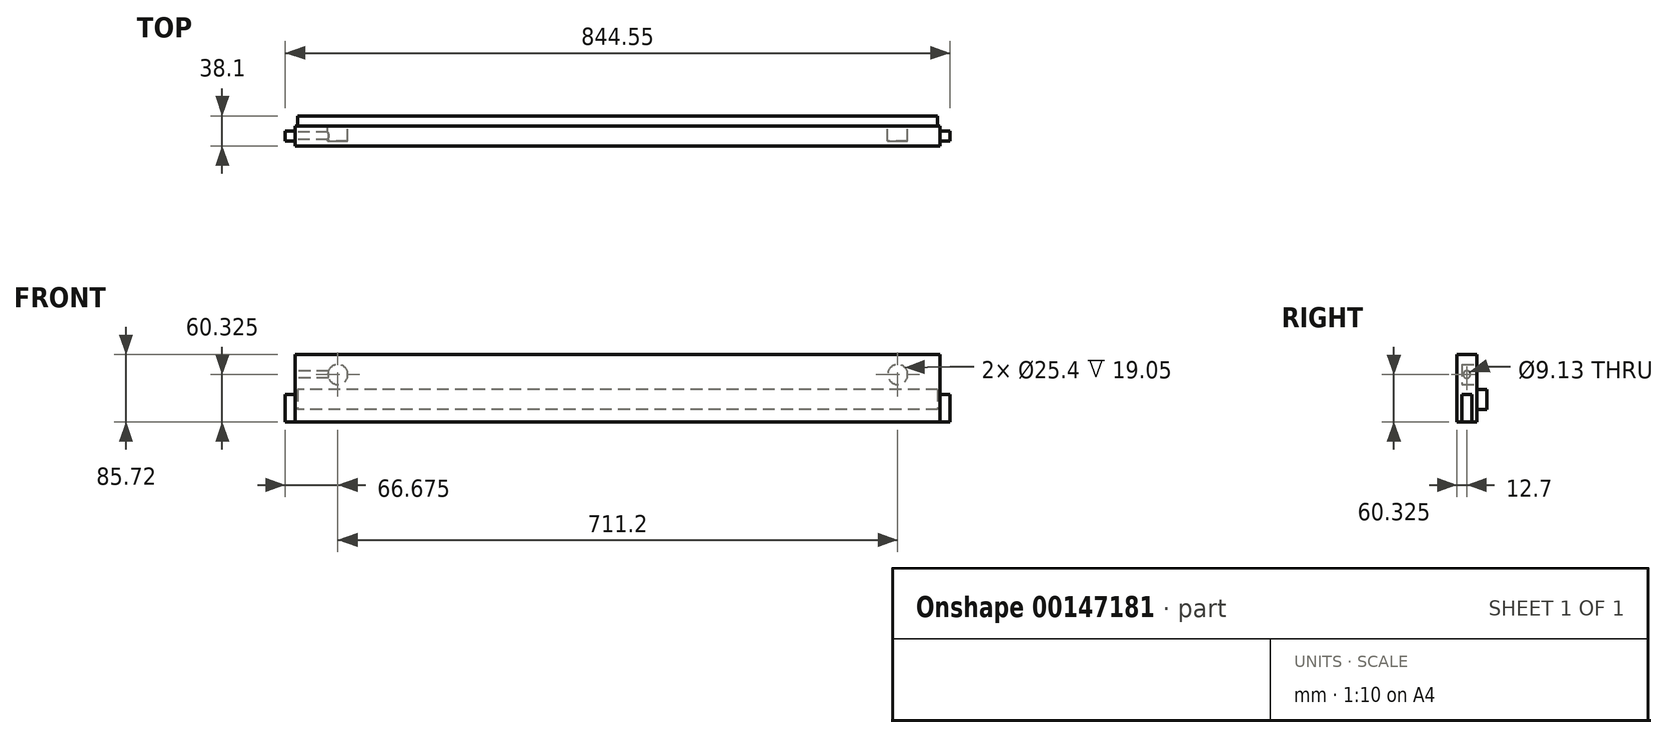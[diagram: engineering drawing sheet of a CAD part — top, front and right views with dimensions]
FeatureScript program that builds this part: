
annotation { "Feature Type Name" : "Feature", "Feature Type Description" : "" }
export const myFeature = defineFeature(function(context is Context, id is Id, definition is map)
    precondition{}
    {
        {
            var Q0;
            Q0=qCreatedBy(makeId("Front.planeOp"),FACE);
            var sketch = newSketch(context, id + "F0", { "sketchPlane" : qUnion([Q0])});
            skLineSegment(sketch, "E0.bottom", {"start": v(0, 0) * mm, "end": v(844.55, 0) * mm});
            skLineSegment(sketch, "E0.top", {"start": v(0, 85.73) * mm, "end": v(844.55, 85.73) * mm});
            skLineSegment(sketch, "E0.left", {"start": v(0, 0) * mm, "end": v(0, 85.73) * mm});
            skLineSegment(sketch, "E0.right", {"start": v(844.55, 0) * mm, "end": v(844.55, 85.73) * mm});
            skSolve(sketch);
        }
        {
            var Q0;
            Q0=makeQuery(id+"F0.imprint","IMPRINT",FACE,{"disambiguationData":[TD([[makeQuery(id+"F0.imprint","IMPRINT",EDGE,{"derivedFrom":sQuery(id+"F0.wireOp",EDGE,"E0.bottom")}),1.0]])]});
            extrude(context, id + "F1", {"entities" : qUnion([Q0]), "depth" : 25.4 * mm});
        }
        {
            var Q0;
            Q0=makeQuery(id+"F1.opExtrude","CAP_FACE",FACE,{"disambiguationData":[OSD([sQuery(id+"F0.wireOp",EDGE,"E0.bottom"),sQuery(id+"F0.wireOp",EDGE,"E0.top"),sQuery(id+"F0.wireOp",EDGE,"E0.left"),sQuery(id+"F0.wireOp",EDGE,"E0.right")])],"isStart":false});
            var sketch = newSketch(context, id + "F2", { "sketchPlane" : qUnion([Q0])});
            skLineSegment(sketch, "E1.bottom", {"start": v(0, 85.73) * mm, "end": v(12.7, 85.73) * mm});
            skLineSegment(sketch, "E1.top", {"start": v(0, 34.93) * mm, "end": v(12.7, 34.93) * mm});
            skLineSegment(sketch, "E1.left", {"start": v(0, 85.73) * mm, "end": v(0, 34.93) * mm});
            skLineSegment(sketch, "E1.right", {"start": v(12.7, 85.73) * mm, "end": v(12.7, 34.92) * mm});
            skLineSegment(sketch, "E2.bottom", {"start": v(831.85, 85.73) * mm, "end": v(844.55, 85.73) * mm});
            skLineSegment(sketch, "E2.top", {"start": v(831.85, 34.92) * mm, "end": v(844.55, 34.92) * mm});
            skLineSegment(sketch, "E2.left", {"start": v(831.85, 85.73) * mm, "end": v(831.85, 34.92) * mm});
            skLineSegment(sketch, "E2.right", {"start": v(844.55, 85.73) * mm, "end": v(844.55, 34.93) * mm});
            skSolve(sketch);
        }
        {
            var Q0;
            Q0=makeQuery(id+"F2.imprint","IMPRINT",FACE,{"disambiguationData":[TD([[makeQuery(id+"F2.imprint","IMPRINT",EDGE,{"derivedFrom":sQuery(id+"F2.wireOp",EDGE,"E1.bottom")}),-1.0]])]});
            var Q1;
            Q1=makeQuery(id+"F2.imprint","IMPRINT",FACE,{"disambiguationData":[TD([[makeQuery(id+"F2.imprint","IMPRINT",EDGE,{"derivedFrom":sQuery(id+"F2.wireOp",EDGE,"E2.bottom")}),-1.0]])]});
            extrude(context, id + "F3", {"entities" : qUnion([Q0, Q1]), "operationType" : NewBodyOperationType.REMOVE, "endBound" : BoundingType.THROUGH_ALL, "oppositeDirection" : true, "depth" : 25.4 * mm});
        }
        {
            var Q0;
            Q0=makeQuery(id+"F1.opExtrude","SWEPT_FACE",FACE,{"disambiguationData":[OSD([sQuery(id+"F0.wireOp",EDGE,"E0.bottom")])]});
            var sketch = newSketch(context, id + "F4", { "sketchPlane" : qUnion([Q0])});
            skLineSegment(sketch, "E3.bottom", {"start": v(0, 25.4) * mm, "end": v(12.7, 25.4) * mm});
            skLineSegment(sketch, "E3.top", {"start": v(0, 19.05) * mm, "end": v(12.7, 19.05) * mm});
            skLineSegment(sketch, "E3.left", {"start": v(0, 25.4) * mm, "end": v(0, 19.05) * mm});
            skLineSegment(sketch, "E3.right", {"start": v(12.7, 25.4) * mm, "end": v(12.7, 19.05) * mm});
            skLineSegment(sketch, "E4.bottom", {"start": v(831.85, 25.4) * mm, "end": v(844.55, 25.4) * mm});
            skLineSegment(sketch, "E4.top", {"start": v(831.85, 19.05) * mm, "end": v(844.55, 19.05) * mm});
            skLineSegment(sketch, "E4.left", {"start": v(831.85, 25.4) * mm, "end": v(831.85, 19.05) * mm});
            skLineSegment(sketch, "E4.right", {"start": v(844.55, 25.4) * mm, "end": v(844.55, 19.05) * mm});
            skLineSegment(sketch, "E5.bottom", {"start": v(0, 6.35) * mm, "end": v(12.7, 6.35) * mm});
            skLineSegment(sketch, "E5.top", {"start": v(0, 0) * mm, "end": v(12.7, 0) * mm});
            skLineSegment(sketch, "E5.left", {"start": v(0, 6.35) * mm, "end": v(0, 0) * mm});
            skLineSegment(sketch, "E5.right", {"start": v(12.7, 6.35) * mm, "end": v(12.7, 0) * mm});
            skLineSegment(sketch, "E6.bottom", {"start": v(831.85, 6.35) * mm, "end": v(844.55, 6.35) * mm});
            skLineSegment(sketch, "E6.top", {"start": v(831.85, 0) * mm, "end": v(844.55, 0) * mm});
            skLineSegment(sketch, "E6.left", {"start": v(831.85, 6.35) * mm, "end": v(831.85, 0) * mm});
            skLineSegment(sketch, "E6.right", {"start": v(844.55, 6.35) * mm, "end": v(844.55, 0) * mm});
            skSolve(sketch);
        }
        {
            var Q0;
            Q0=makeQuery(id+"F4.imprint","IMPRINT",FACE,{"disambiguationData":[TD([[makeQuery(id+"F4.imprint","IMPRINT",EDGE,{"derivedFrom":sQuery(id+"F4.wireOp",EDGE,"E4.bottom")}),-1.0]])]});
            var Q1;
            Q1=makeQuery(id+"F4.imprint","IMPRINT",FACE,{"disambiguationData":[TD([[makeQuery(id+"F4.imprint","IMPRINT",EDGE,{"derivedFrom":sQuery(id+"F4.wireOp",EDGE,"E6.bottom")}),-1.0]])]});
            var Q2;
            Q2=makeQuery(id+"F4.imprint","IMPRINT",FACE,{"disambiguationData":[TD([[makeQuery(id+"F4.imprint","IMPRINT",EDGE,{"derivedFrom":sQuery(id+"F4.wireOp",EDGE,"E3.bottom")}),-1.0]])]});
            var Q3;
            Q3=makeQuery(id+"F4.imprint","IMPRINT",FACE,{"disambiguationData":[TD([[makeQuery(id+"F4.imprint","IMPRINT",EDGE,{"derivedFrom":sQuery(id+"F4.wireOp",EDGE,"E5.bottom")}),-1.0]])]});
            extrude(context, id + "F5", {"entities" : qUnion([Q0, Q1, Q2, Q3]), "operationType" : NewBodyOperationType.REMOVE, "endBound" : BoundingType.THROUGH_ALL, "oppositeDirection" : true, "depth" : 25.4 * mm});
        }
        {
            var Q0;
            Q0=makeQuery(id+"F5.boolean.opBoolean","MERGE",FACE,{"derivedFrom":[makeQuery(id+"F3.boolean.opBoolean","COPY",FACE,{"derivedFrom":makeQuery(id+"F3.opExtrude","SWEPT_FACE",FACE,{"disambiguationData":[OSD([sQuery(id+"F2.wireOp",EDGE,"E1.right")])]})}),makeQuery(id+"F5.opExtrude","SWEPT_FACE",FACE,{"disambiguationData":[OSD([sQuery(id+"F4.wireOp",EDGE,"E3.right")])]}),makeQuery(id+"F5.opExtrude","SWEPT_FACE",FACE,{"disambiguationData":[OSD([sQuery(id+"F4.wireOp",EDGE,"E5.right")])]})]});
            var sketch = newSketch(context, id + "F6", { "sketchPlane" : qUnion([Q0])});
            skCircle(sketch, "E7", {"center": v(12.7, 60.33) * mm, "radius": 4.56 * mm});
            skPoint(sketch, "E7.centerSnap0", {"position": v(12.7, 85.73) * mm});
            skSolve(sketch);
        }
        {
            var Q0;
            Q0=makeQuery(id+"F6.imprint","IMPRINT",FACE,{"disambiguationData":[TD([[makeQuery(id+"F6.imprint","IMPRINT",EDGE,{"derivedFrom":sQuery(id+"F6.wireOp",EDGE,"E7")}),1.0]])]});
            extrude(context, id + "F7", {"entities" : qUnion([Q0]), "operationType" : NewBodyOperationType.REMOVE, "oppositeDirection" : true, "depth" : 50.8 * mm});
        }
        {
            var Q0;
            Q0=makeQuery(id+"F1.opExtrude","CAP_FACE",FACE,{"disambiguationData":[OSD([sQuery(id+"F0.wireOp",EDGE,"E0.bottom"),sQuery(id+"F0.wireOp",EDGE,"E0.top"),sQuery(id+"F0.wireOp",EDGE,"E0.left"),sQuery(id+"F0.wireOp",EDGE,"E0.right")])],"isStart":true});
            var sketch = newSketch(context, id + "F8", { "sketchPlane" : qUnion([Q0])});
            skCircle(sketch, "E8", {"center": v(-66.67, 60.33) * mm, "radius": 12.7 * mm});
            skCircle(sketch, "E9", {"center": v(-777.88, 60.33) * mm, "radius": 12.7 * mm});
            skSolve(sketch);
        }
        {
            var Q0;
            Q0=makeQuery(id+"F8.imprint","IMPRINT",FACE,{"disambiguationData":[TD([[makeQuery(id+"F8.imprint","IMPRINT",EDGE,{"derivedFrom":sQuery(id+"F8.wireOp",EDGE,"E8")}),1.0]])]});
            var Q1;
            Q1=makeQuery(id+"F8.imprint","IMPRINT",FACE,{"disambiguationData":[TD([[makeQuery(id+"F8.imprint","IMPRINT",EDGE,{"derivedFrom":sQuery(id+"F8.wireOp",EDGE,"E9")}),1.0]])]});
            extrude(context, id + "F9", {"entities" : qUnion([Q0, Q1]), "operationType" : NewBodyOperationType.REMOVE, "oppositeDirection" : true, "depth" : 19.05 * mm});
        }
        {
            var Q0;
            Q0=makeQuery(id+"F1.opExtrude","CAP_FACE",FACE,{"disambiguationData":[OSD([sQuery(id+"F0.wireOp",EDGE,"E0.bottom"),sQuery(id+"F0.wireOp",EDGE,"E0.top"),sQuery(id+"F0.wireOp",EDGE,"E0.left"),sQuery(id+"F0.wireOp",EDGE,"E0.right")])],"isStart":true});
            var sketch = newSketch(context, id + "F10", { "sketchPlane" : qUnion([Q0])});
            skLineSegment(sketch, "E10.bottom", {"start": v(-828.68, 41.28) * mm, "end": v(-15.87, 41.28) * mm});
            skLineSegment(sketch, "E10.top", {"start": v(-828.68, 15.88) * mm, "end": v(-15.87, 15.88) * mm});
            skLineSegment(sketch, "E10.left", {"start": v(-828.68, 41.28) * mm, "end": v(-828.68, 15.88) * mm});
            skLineSegment(sketch, "E10.right", {"start": v(-15.87, 41.28) * mm, "end": v(-15.87, 15.88) * mm});
            skSolve(sketch);
        }
        {
            var Q0;
            Q0=makeQuery(id+"F10.imprint","IMPRINT",FACE,{"disambiguationData":[TD([[makeQuery(id+"F10.imprint","IMPRINT",EDGE,{"derivedFrom":sQuery(id+"F10.wireOp",EDGE,"E10.bottom")}),-1.0]])]});
            extrude(context, id + "F11", {"entities" : qUnion([Q0]), "operationType" : NewBodyOperationType.ADD, "depth" : 12.7 * mm});
        }
    });
